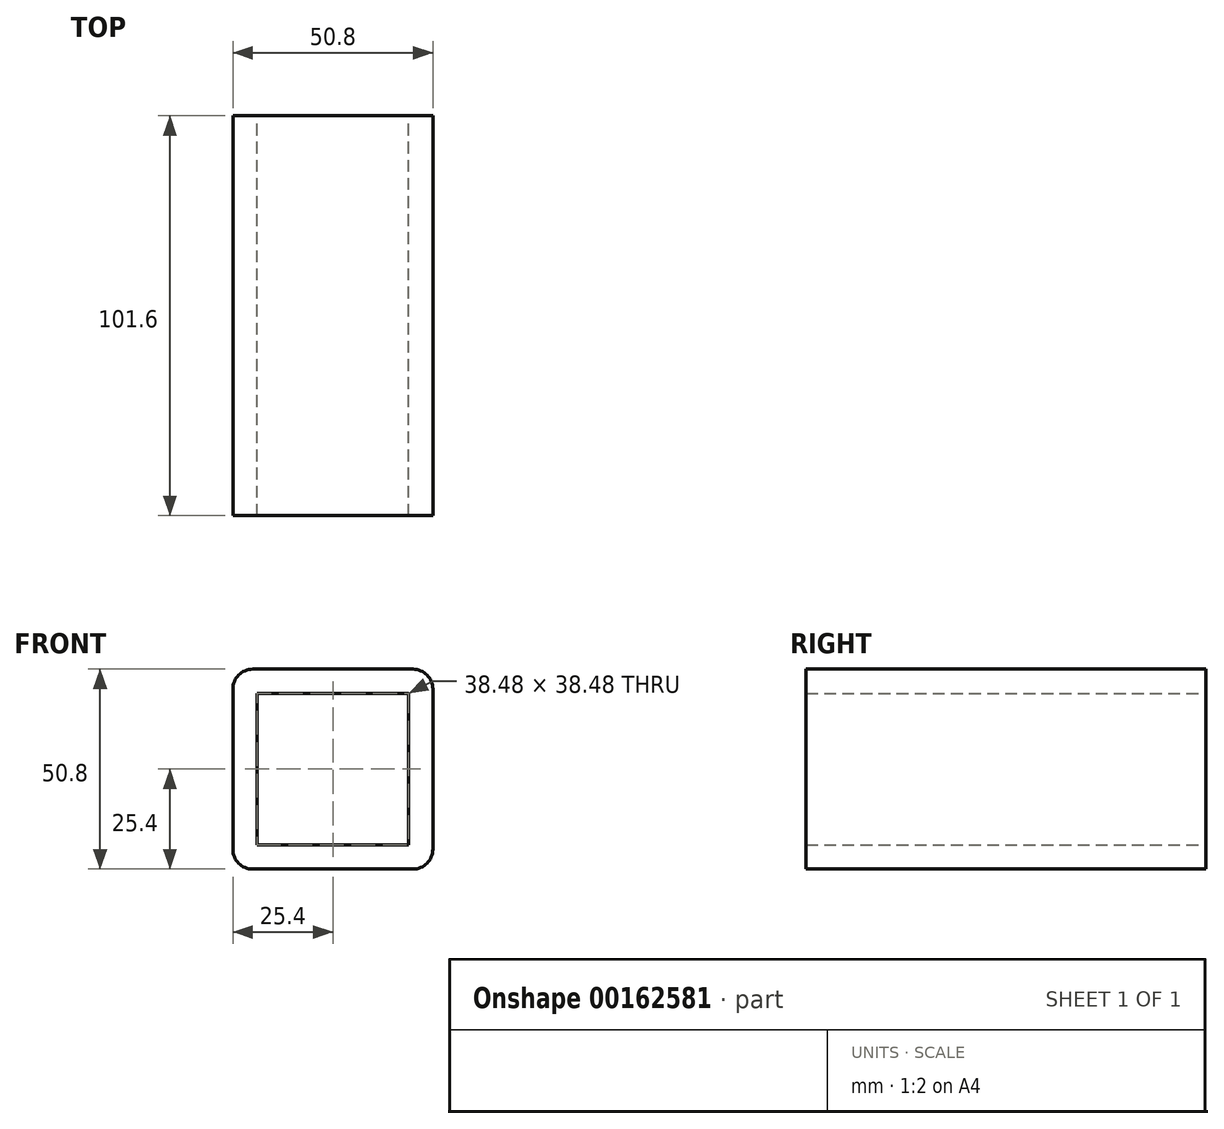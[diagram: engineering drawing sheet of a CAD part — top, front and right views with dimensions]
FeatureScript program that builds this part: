
annotation { "Feature Type Name" : "Feature", "Feature Type Description" : "" }
export const myFeature = defineFeature(function(context is Context, id is Id, definition is map)
    precondition{}
    {
        {
            var Q0;
            Q0=qCreatedBy(makeId("Front.planeOp"),FACE);
            var sketch = newSketch(context, id + "F0", { "sketchPlane" : qUnion([Q0])});
            skLineSegment(sketch, "E0.bottom", {"start": v(19.24, 19.24) * mm, "end": v(-19.24, 19.24) * mm});
            skLineSegment(sketch, "E0.top", {"start": v(19.24, -19.24) * mm, "end": v(-19.24, -19.24) * mm});
            skLineSegment(sketch, "E0.left", {"start": v(19.24, 19.24) * mm, "end": v(19.24, -19.24) * mm});
            skLineSegment(sketch, "E0.right", {"start": v(-19.24, 19.24) * mm, "end": v(-19.24, -19.24) * mm});
            skPoint(sketch, "E0.middle", {"position": v(0, 0) * mm});
            skLineSegment(sketch, "E1.0", {"start": v(-25.4, 25.4) * mm, "end": v(-25.4, -25.4) * mm});
            skLineSegment(sketch, "E1.1", {"start": v(25.4, 25.4) * mm, "end": v(-25.4, 25.4) * mm});
            skLineSegment(sketch, "E1.2", {"start": v(25.4, 25.4) * mm, "end": v(25.4, -25.4) * mm});
            skLineSegment(sketch, "E1.3", {"start": v(25.4, -25.4) * mm, "end": v(-25.4, -25.4) * mm});
            skSolve(sketch);
        }
        {
            var Q0;
            Q0=makeQuery(id+"F0.imprint","IMPRINT",FACE,{"disambiguationData":[TD([[makeQuery(id+"F0.imprint","IMPRINT",EDGE,{"derivedFrom":sQuery(id+"F0.wireOp",EDGE,"E0.bottom")}),-1.0]])]});
            extrude(context, id + "F1", {"entities" : qUnion([Q0]), "depth" : 101.6 * mm});
        }
        {
            var Q0;
            Q0=makeQuery(id+"F1.opExtrude","SWEPT_EDGE",EDGE,{"disambiguationData":[OSD([sQuery(id+"F0.wireOp",EDGE,"E1.0"),sQuery(id+"F0.wireOp",EDGE,"E1.1")])]});
            var Q1;
            Q1=makeQuery(id+"F1.opExtrude","SWEPT_EDGE",EDGE,{"disambiguationData":[OSD([sQuery(id+"F0.wireOp",EDGE,"E1.0"),sQuery(id+"F0.wireOp",EDGE,"E1.3")])]});
            var Q2;
            Q2=makeQuery(id+"F1.opExtrude","SWEPT_EDGE",EDGE,{"disambiguationData":[OSD([sQuery(id+"F0.wireOp",EDGE,"E1.2"),sQuery(id+"F0.wireOp",EDGE,"E1.3")])]});
            var Q3;
            Q3=makeQuery(id+"F1.opExtrude","SWEPT_EDGE",EDGE,{"disambiguationData":[OSD([sQuery(id+"F0.wireOp",EDGE,"E1.1"),sQuery(id+"F0.wireOp",EDGE,"E1.2")])]});
            fillet(context, id + "F2", {"entities" : qUnion([Q0, Q1, Q2, Q3]), "radius" : 5.08 * mm, "tangentPropagation" : true, "allowEdgeOverflow" : false});
        }
    });
